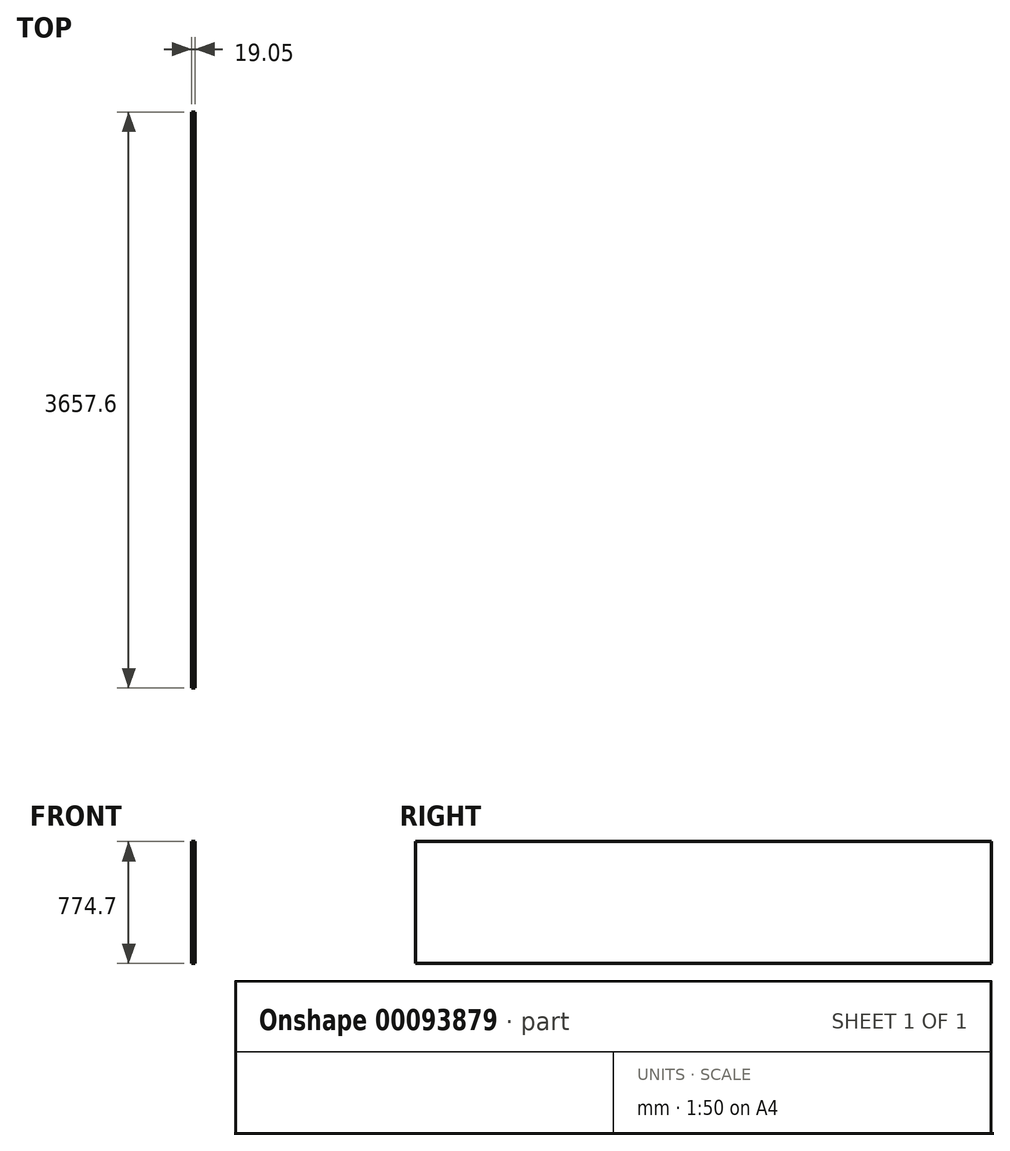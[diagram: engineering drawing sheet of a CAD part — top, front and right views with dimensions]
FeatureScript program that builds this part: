
annotation { "Feature Type Name" : "Feature", "Feature Type Description" : "" }
export const myFeature = defineFeature(function(context is Context, id is Id, definition is map)
    precondition{}
    {
        {
            var Q0;
            Q0=qCreatedBy(makeId("Right.planeOp"),FACE);
            var sketch = newSketch(context, id + "F0", { "sketchPlane" : qUnion([Q0])});
            skLineSegment(sketch, "E0.bottom", {"start": v(-1828.8, 774.7) * mm, "end": v(1828.8, 774.7) * mm});
            skLineSegment(sketch, "E0.top", {"start": v(-1828.8, 0) * mm, "end": v(1828.8, 0) * mm});
            skLineSegment(sketch, "E0.left", {"start": v(-1828.8, 774.7) * mm, "end": v(-1828.8, 0) * mm});
            skLineSegment(sketch, "E0.right", {"start": v(1828.8, 774.7) * mm, "end": v(1828.8, 0) * mm});
            skSolve(sketch);
        }
        {
            var Q0;
            Q0 = qSketchRegion(id + "F0", true);
            extrude(context, id + "F1", {"entities" : qUnion([Q0]), "depth" : 19.05 * mm});
        }
    });
